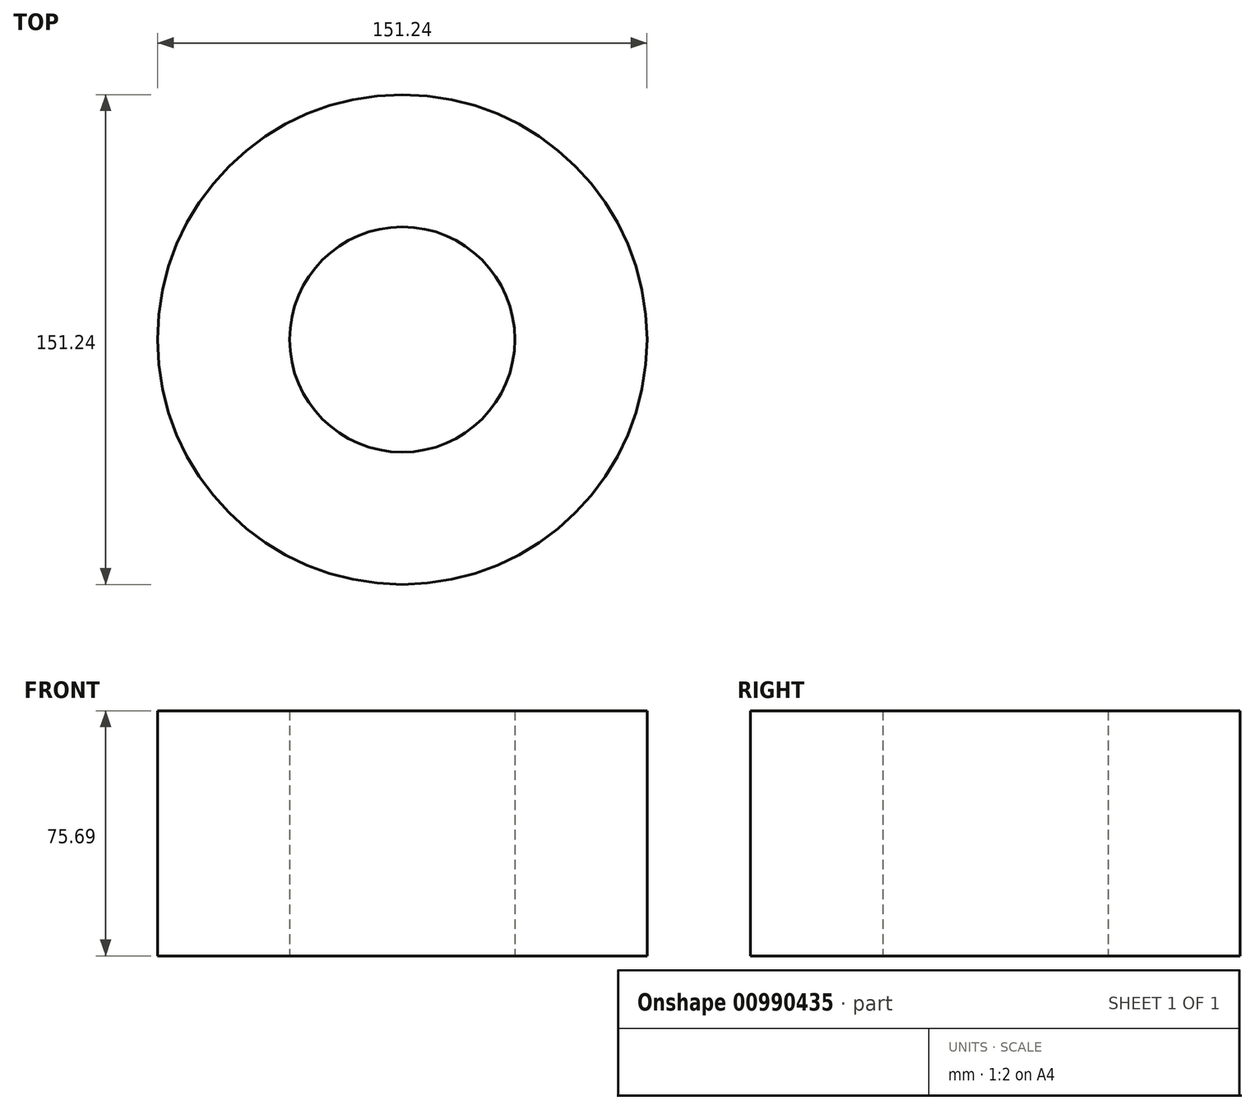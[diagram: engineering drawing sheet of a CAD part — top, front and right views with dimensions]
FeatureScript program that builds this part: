
annotation { "Feature Type Name" : "Feature", "Feature Type Description" : "" }
export const myFeature = defineFeature(function(context is Context, id is Id, definition is map)
    precondition{}
    {
        {
            var Q0;
            Q0=qCreatedBy(makeId("Top.planeOp"),FACE);
            var sketch = newSketch(context, id + "F0", { "sketchPlane" : qUnion([Q0])});
            skCircle(sketch, "E0", {"center": v(0, 0) * mm, "radius": 75.62 * mm});
            skSolve(sketch);
        }
        {
            var Q0;
            Q0=makeQuery(id+"F0.imprint","IMPRINT",FACE,{"disambiguationData":[TD([[makeQuery(id+"F0.imprint","IMPRINT",EDGE,{"derivedFrom":sQuery(id+"F0.wireOp",EDGE,"E0")}),1.0]])]});
            extrude(context, id + "F1", {"entities" : qUnion([Q0]), "depth" : 75.7 * mm, "offsetDistance" : 25.4 * mm});
        }
        {
            var Q0;
            Q0=makeQuery(id+"F1.opExtrude","CAP_FACE",FACE,{"disambiguationData":[OSD([sQuery(id+"F0.wireOp",EDGE,"E0")])],"isStart":false});
            var sketch = newSketch(context, id + "F2", { "sketchPlane" : qUnion([Q0])});
            skCircle(sketch, "E1", {"center": v(0, 0) * mm, "radius": 34.79 * mm});
            skSolve(sketch);
        }
        {
            var Q0;
            Q0=makeQuery(id+"F2.imprint","IMPRINT",FACE,{"disambiguationData":[TD([[makeQuery(id+"F2.imprint","IMPRINT",EDGE,{"derivedFrom":sQuery(id+"F2.wireOp",EDGE,"E1")}),1.0]])]});
            extrude(context, id + "F3", {"entities" : qUnion([Q0]), "operationType" : NewBodyOperationType.ADD, "oppositeDirection" : true, "depth" : 148.84 * mm, "offsetDistance" : 25.4 * mm});
        }
        {
            var Q0;
            Q0=makeQuery(id+"F3.opExtrude","CAP_FACE",FACE,{"disambiguationData":[OSD([sQuery(id+"F2.wireOp",EDGE,"E1")])],"isStart":false});
            extrude(context, id + "F4", {"entities" : qUnion([Q0]), "operationType" : NewBodyOperationType.REMOVE, "oppositeDirection" : true, "depth" : 287.27 * mm, "offsetDistance" : 25.4 * mm});
        }
    });
